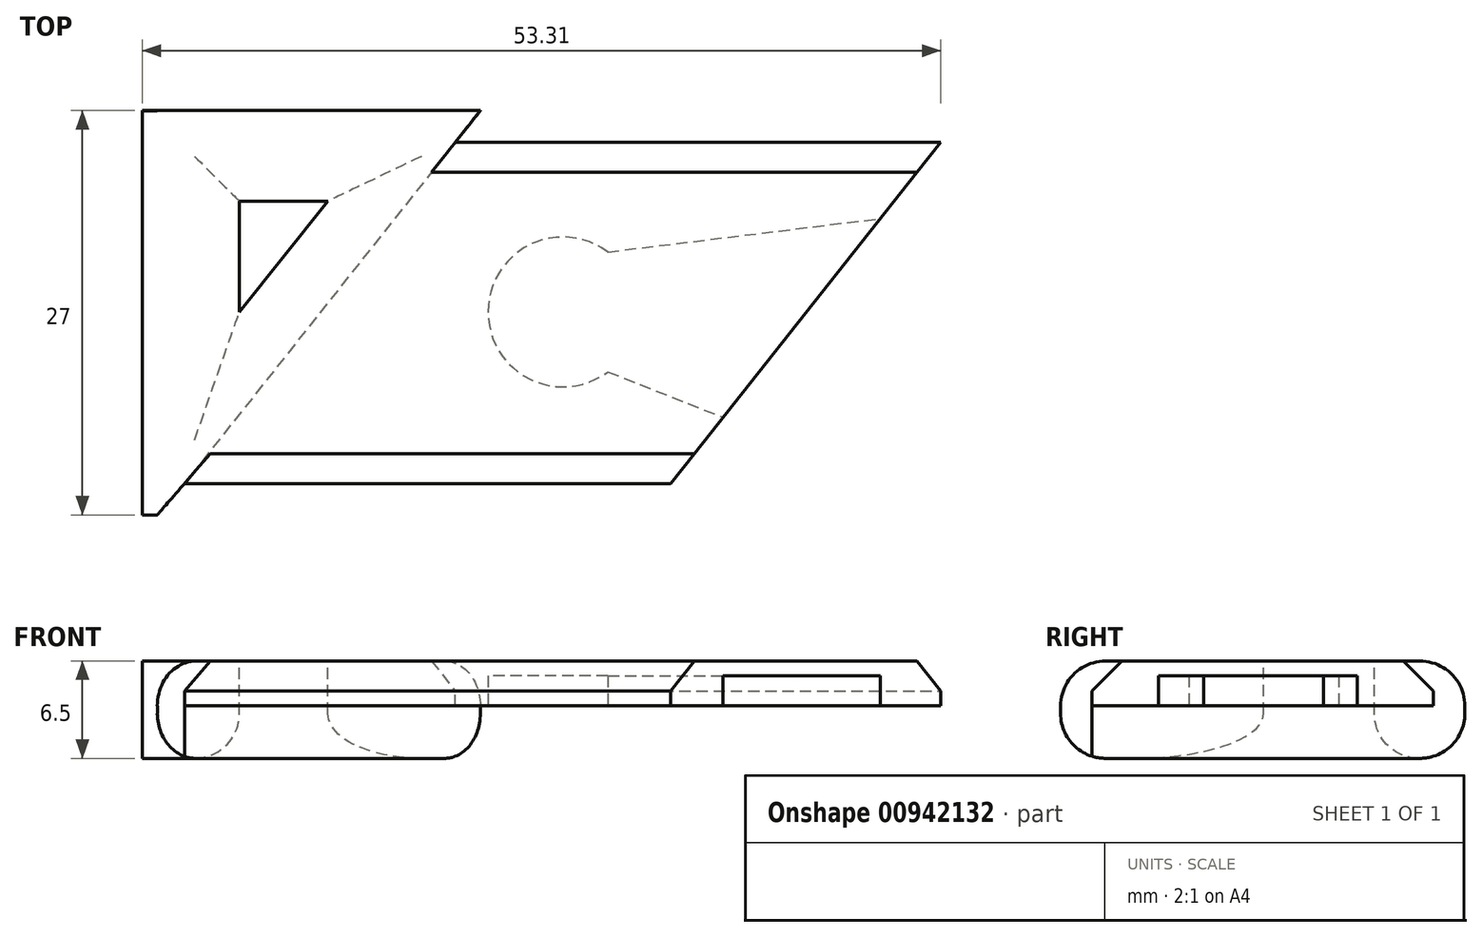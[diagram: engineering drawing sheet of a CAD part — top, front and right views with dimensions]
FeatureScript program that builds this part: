
annotation { "Feature Type Name" : "Feature", "Feature Type Description" : "" }
export const myFeature = defineFeature(function(context is Context, id is Id, definition is map)
    precondition{}
    {
        {
            var Q0;
            Q0=qCreatedBy(makeId("Top.planeOp"),FACE);
            var sketch = newSketch(context, id + "F0", { "sketchPlane" : qUnion([Q0])});
            skLineSegment(sketch, "E0", {"start": v(26.99, 13.44) * mm, "end": v(-5.51, 13.44) * mm, "construction": true});
            skLineSegment(sketch, "E1", {"start": v(-5.51, 13.44) * mm, "end": v(-8.7, 9.44) * mm, "construction": true});
            skLineSegment(sketch, "E2", {"start": v(-8.7, 9.44) * mm, "end": v(23.8, 9.44) * mm, "construction": true});
            skLineSegment(sketch, "E3", {"start": v(23.8, 9.44) * mm, "end": v(26.99, 13.44) * mm, "construction": true});
            skLineSegment(sketch, "E4", {"start": v(-27.08, -13.56) * mm, "end": v(5.43, -13.56) * mm, "construction": true});
            skLineSegment(sketch, "E5", {"start": v(5.43, -13.56) * mm, "end": v(8.61, -9.56) * mm, "construction": true});
            skLineSegment(sketch, "E6", {"start": v(8.61, -9.56) * mm, "end": v(-23.83, -9.56) * mm, "construction": true});
            skLineSegment(sketch, "E7", {"start": v(-23.83, -9.56) * mm, "end": v(-27.08, -13.56) * mm, "construction": true});
            skLineSegment(sketch, "E8", {"start": v(-7.18, 11.34) * mm, "end": v(25.23, 11.34) * mm, "construction": true});
            skLineSegment(sketch, "E9", {"start": v(-25.27, -11.46) * mm, "end": v(7.18, -11.46) * mm, "construction": true});
            skLineSegment(sketch, "E10", {"start": v(-27.08, -13.56) * mm, "end": v(-27.08, 13.44) * mm});
            skLineSegment(sketch, "E11", {"start": v(-27.08, 13.44) * mm, "end": v(-5.51, 13.44) * mm});
            skLineSegment(sketch, "E12", {"start": v(-7.18, 11.34) * mm, "end": v(25.23, 11.34) * mm});
            skLineSegment(sketch, "E13", {"start": v(7.18, -11.46) * mm, "end": v(25.23, 11.34) * mm});
            skLineSegment(sketch, "E14", {"start": v(7.18, -11.46) * mm, "end": v(-25.27, -11.46) * mm});
            skLineSegment(sketch, "E15", {"start": v(-7.18, 11.34) * mm, "end": v(-25.27, -11.46) * mm});
            skLineSegment(sketch, "E16", {"start": v(-5.51, 13.44) * mm, "end": v(-7.18, 11.34) * mm});
            skLineSegment(sketch, "E17", {"start": v(-27.08, -13.56) * mm, "end": v(-25.27, -11.46) * mm});
            skLineSegment(sketch, "E18", {"start": v(-27.08, 13.44) * mm, "end": v(-28.08, 13.44) * mm});
            skLineSegment(sketch, "E19", {"start": v(-28.08, 13.44) * mm, "end": v(-28.08, -13.56) * mm});
            skLineSegment(sketch, "E20", {"start": v(-28.08, -13.56) * mm, "end": v(-27.08, -13.56) * mm});
            skSolve(sketch);
        }
        {
            var Q0;
            Q0=qCreatedBy(makeId("Top.planeOp"),FACE);
            var sketch = newSketch(context, id + "F1", { "sketchPlane" : qUnion([Q0])});
            skLineSegment(sketch, "E21", {"start": v(-27.08, -13.56) * mm, "end": v(-27.08, 13.44) * mm});
            skLineSegment(sketch, "E22", {"start": v(-27.08, 13.44) * mm, "end": v(-5.51, 13.44) * mm});
            skLineSegment(sketch, "E23", {"start": v(-5.51, 13.44) * mm, "end": v(-27.08, -13.56) * mm});
            skLineSegment(sketch, "E24", {"start": v(-21.6, 7.39) * mm, "end": v(-15.7, 7.39) * mm});
            skLineSegment(sketch, "E25", {"start": v(-15.7, 7.39) * mm, "end": v(-21.6, 0) * mm});
            skLineSegment(sketch, "E26", {"start": v(-21.6, 0) * mm, "end": v(-21.6, 7.39) * mm});
            skLineSegment(sketch, "E27", {"start": v(-27.08, 13.44) * mm, "end": v(-28.08, 13.44) * mm});
            skLineSegment(sketch, "E28", {"start": v(-28.08, 13.44) * mm, "end": v(-28.08, -13.56) * mm});
            skLineSegment(sketch, "E29", {"start": v(-28.08, -13.56) * mm, "end": v(-27.08, -13.56) * mm});
            skSolve(sketch);
        }
        {
            var Q0;
            Q0=makeQuery(id+"F0.imprint","IMPRINT",FACE,{"disambiguationData":[TD([[makeQuery(id+"F0.imprint","IMPRINT",EDGE,{"derivedFrom":sQuery(id+"F0.wireOp",EDGE,"E10")}),-1.0]])]});
            var Q1;
            Q1=makeQuery(id+"F0.imprint","IMPRINT",FACE,{"disambiguationData":[TD([[makeQuery(id+"F0.imprint","IMPRINT",EDGE,{"derivedFrom":sQuery(id+"F0.wireOp",EDGE,"E12")}),-1.0]])]});
            var Q2;
            Q2=makeQuery(id+"F0.imprint","IMPRINT",FACE,{"disambiguationData":[TD([[makeQuery(id+"F0.imprint","IMPRINT",EDGE,{"derivedFrom":sQuery(id+"F0.wireOp",EDGE,"E10")}),1.0]])]});
            extrude(context, id + "F2", {"entities" : qUnion([Q0, Q1, Q2]), "oppositeDirection" : true, "depth" : 3 * mm, "offsetDistance" : 25 * mm});
        }
        {
            var Q0;
            Q0=makeQuery(id+"F0.imprint","IMPRINT",FACE,{"disambiguationData":[TD([[makeQuery(id+"F0.imprint","IMPRINT",EDGE,{"derivedFrom":sQuery(id+"F0.wireOp",EDGE,"E10")}),-1.0]])]});
            var Q1;
            Q1 = qSketchRegion(id + "F1", true);
            extrude(context, id + "F3", {"entities" : qUnion([Q0, Q1]), "operationType" : NewBodyOperationType.ADD, "oppositeDirection" : true, "depth" : 6.5 * mm, "offsetDistance" : 25 * mm});
        }
        {
            var Q0;
            Q0=makeQuery(id+"F2.opExtrude","CAP_EDGE",EDGE,{"disambiguationData":[OSD([sQuery(id+"F0.wireOp",EDGE,"E12")])],"isStart":true});
            var Q1;
            Q1=makeQuery(id+"F2.opExtrude","CAP_EDGE",EDGE,{"disambiguationData":[OSD([sQuery(id+"F0.wireOp",EDGE,"E14")])],"isStart":true});
            chamfer(context, id + "F4", {"entities" : qUnion([Q0, Q1]), "width" : 2 * mm, "tangentPropagation" : true});
        }
        {
            var Q0;
            Q0=makeQuery(id+"F2.opExtrude","CAP_EDGE",EDGE,{"disambiguationData":[OSD([sQuery(id+"F0.wireOp",EDGE,"E11")])],"isStart":true});
            var Q1;
            Q1=makeQuery(id+"F3.opExtrude","CAP_EDGE",EDGE,{"disambiguationData":[OSD([sQuery(id+"F0.wireOp",EDGE,"E11")])],"isStart":false});
            var Q2;
            Q2=makeQuery(id+"F2.opExtrude","CAP_EDGE",EDGE,{"disambiguationData":[OSD([sQuery(id+"F0.wireOp",EDGE,"7gGAPOjL-t7sV-ewJa-ArCT-nc4j6WmRso13")])],"isStart":true});
            var Q3;
            Q3=makeQuery(id+"F2.opExtrude","CAP_EDGE",EDGE,{"disambiguationData":[OSD([sQuery(id+"F0.wireOp",EDGE,"yde29xXl-ICFn-0QiE-HzA1-EqmZUxvuQBXi")])],"isStart":true});
            var Q4;
            Q4=makeQuery(id+"F2.opExtrude","CAP_EDGE",EDGE,{"disambiguationData":[OSD([sQuery(id+"F0.wireOp",EDGE,"CeoQsM6z-U6Wm-WrTS-g2a8-tBGnORVz6SGF")])],"isStart":true});
            var Q5;
            Q5=makeQuery(id+"F3.opExtrude","CAP_EDGE",EDGE,{"disambiguationData":[OSD([sQuery(id+"F0.wireOp",EDGE,"7gGAPOjL-t7sV-ewJa-ArCT-nc4j6WmRso13")])],"isStart":false});
            var Q6;
            Q6=makeQuery(id+"F3.opExtrude","CAP_EDGE",EDGE,{"disambiguationData":[OSD([sQuery(id+"F0.wireOp",EDGE,"CeoQsM6z-U6Wm-WrTS-g2a8-tBGnORVz6SGF")])],"isStart":false});
            var Q7;
            Q7=makeQuery(id+"F3.opExtrude","CAP_EDGE",EDGE,{"disambiguationData":[OSD([sQuery(id+"F0.wireOp",EDGE,"yde29xXl-ICFn-0QiE-HzA1-EqmZUxvuQBXi")])],"isStart":false});
            var Q8;
            Q8=makeQuery(id+"F3.opExtrude","CAP_EDGE",EDGE,{"disambiguationData":[OSD([sQuery(id+"F1.wireOp",EDGE,"E29")])],"isStart":false});
            var Q9;
            Q9=makeQuery(id+"F2.opExtrude","CAP_EDGE",EDGE,{"disambiguationData":[OSD([sQuery(id+"F0.wireOp",EDGE,"E20")])],"isStart":true});
            fillet(context, id + "F5", {"entities" : qUnion([Q0, Q1, Q2, Q3, Q4, Q5, Q6, Q7, Q8, Q9]), "radius" : 3 * mm, "tangentPropagation" : true, "allowEdgeOverflow" : false});
        }
        {
            var Q0;
            Q0=makeQuery(id+"F1.imprint","IMPRINT",FACE,{"disambiguationData":[TD([[makeQuery(id+"F1.imprint","IMPRINT",EDGE,{"derivedFrom":sQuery(id+"F1.wireOp",EDGE,"E24")}),-1.0]])]});
            extrude(context, id + "F6", {"entities" : qUnion([Q0]), "operationType" : NewBodyOperationType.REMOVE, "endBound" : BoundingType.THROUGH_ALL, "oppositeDirection" : true, "depth" : 25 * mm, "offsetDistance" : 25 * mm});
        }
        {
            var Q0;
            Q0=makeQuery(id+"F6.boolean.opBoolean","COPY",EDGE,{"derivedFrom":makeQuery(id+"F6.opExtrude","CAP_EDGE",EDGE,{"disambiguationData":[OSD([sQuery(id+"F1.wireOp",EDGE,"E25")])],"isStart":true})});
            var Q1;
            Q1=makeQuery(id+"F6.boolean.opBoolean","COPY",EDGE,{"derivedFrom":makeQuery(id+"F6.opExtrude","CAP_EDGE",EDGE,{"disambiguationData":[OSD([sQuery(id+"F1.wireOp",EDGE,"E24")])],"isStart":true})});
            var Q2;
            Q2=makeQuery(id+"F6.boolean.opBoolean","COPY",EDGE,{"derivedFrom":makeQuery(id+"F6.opExtrude","CAP_EDGE",EDGE,{"disambiguationData":[OSD([sQuery(id+"F1.wireOp",EDGE,"E26")])],"isStart":true})});
            var Q3;
            Q3=makeQuery(id+"F6.boolean.opBoolean","INTERSECT",EDGE,{"derivedFrom":[makeQuery(id+"F3.opExtrude","CAP_FACE",FACE,{"disambiguationData":[OSD([sQuery(id+"F0.wireOp",EDGE,"E10"),sQuery(id+"F0.wireOp",EDGE,"E11"),sQuery(id+"F0.wireOp",EDGE,"E15"),sQuery(id+"F0.wireOp",EDGE,"E16"),sQuery(id+"F0.wireOp",EDGE,"E17")])],"isStart":false}),makeQuery(id+"F6.opExtrude","SWEPT_FACE",FACE,{"disambiguationData":[OSD([sQuery(id+"F1.wireOp",EDGE,"E24")])]})]});
            var Q4;
            Q4=makeQuery(id+"F6.boolean.opBoolean","INTERSECT",EDGE,{"derivedFrom":[makeQuery(id+"F3.opExtrude","CAP_FACE",FACE,{"disambiguationData":[OSD([sQuery(id+"F0.wireOp",EDGE,"E10"),sQuery(id+"F0.wireOp",EDGE,"E11"),sQuery(id+"F0.wireOp",EDGE,"E15"),sQuery(id+"F0.wireOp",EDGE,"E16"),sQuery(id+"F0.wireOp",EDGE,"E17")])],"isStart":false}),makeQuery(id+"F6.opExtrude","SWEPT_FACE",FACE,{"disambiguationData":[OSD([sQuery(id+"F1.wireOp",EDGE,"E26")])]})]});
            var Q5;
            Q5=makeQuery(id+"F6.boolean.opBoolean","INTERSECT",EDGE,{"derivedFrom":[makeQuery(id+"F3.opExtrude","CAP_FACE",FACE,{"disambiguationData":[OSD([sQuery(id+"F0.wireOp",EDGE,"E10"),sQuery(id+"F0.wireOp",EDGE,"E11"),sQuery(id+"F0.wireOp",EDGE,"E15"),sQuery(id+"F0.wireOp",EDGE,"E16"),sQuery(id+"F0.wireOp",EDGE,"E17")])],"isStart":false}),makeQuery(id+"F6.opExtrude","SWEPT_FACE",FACE,{"disambiguationData":[OSD([sQuery(id+"F1.wireOp",EDGE,"E25")])]})]});
            fillet(context, id + "F7", {"entities" : qUnion([Q0, Q1, Q2, Q3, Q4, Q5]), "radius" : 3 * mm, "tangentPropagation" : true, "allowEdgeOverflow" : false});
        }
        {
            var Q0;
            Q0=makeQuery(id+"F2.opExtrude","CAP_FACE",FACE,{"disambiguationData":[OSD([sQuery(id+"F0.wireOp",EDGE,"E10"),sQuery(id+"F0.wireOp",EDGE,"E11"),sQuery(id+"F0.wireOp",EDGE,"E12"),sQuery(id+"F0.wireOp",EDGE,"E13"),sQuery(id+"F0.wireOp",EDGE,"E14"),sQuery(id+"F0.wireOp",EDGE,"E16"),sQuery(id+"F0.wireOp",EDGE,"E17")])],"isStart":false});
            var sketch = newSketch(context, id + "F8", { "sketchPlane" : qUnion([Q0])});
            skCircle(sketch, "E30", {"center": v(0, 0) * mm, "radius": 5 * mm});
            skLineSegment(sketch, "E31", {"start": v(3, 4) * mm, "end": v(10.68, 7.04) * mm});
            skLineSegment(sketch, "E32", {"start": v(3, -4) * mm, "end": v(21.19, -6.23) * mm});
            skLineSegment(sketch, "E33", {"start": v(21.19, -6.23) * mm, "end": v(10.68, 7.04) * mm});
            skSolve(sketch);
        }
        {
            var Q0;
            {var subQ0=sQuery(id+"F8.wireOp",EDGE,"E31");Q0=makeQuery(id+"F8.imprint","IMPRINT",FACE,{"disambiguationData":[TD([[makeQuery(id+"F8.imprint","IMPRINT",EDGE,{"derivedFrom":subQ0}),-1.0]])]});}
            var Q1;
            {var subQ0=sQuery(id+"F8.wireOp",EDGE,"E30");var subQ1=makeQuery(id+"F8.imprint","INTERSECT",VERTEX,{"derivedFrom":[subQ0,sQuery(id+"F8.wireOp",EDGE,"E31")]});Q1=makeQuery(id+"F8.imprint","IMPRINT",FACE,{"disambiguationData":[TD([[makeQuery(id+"F8.imprint","IMPRINT",EDGE,{"disambiguationData":[TD([[subQ1,-1.0]])],"derivedFrom":subQ0}),1.0]])]});}
            extrude(context, id + "F9", {"entities" : qUnion([Q0, Q1]), "operationType" : NewBodyOperationType.REMOVE, "oppositeDirection" : true, "depth" : 2 * mm, "offsetDistance" : 25 * mm});
        }
    });
